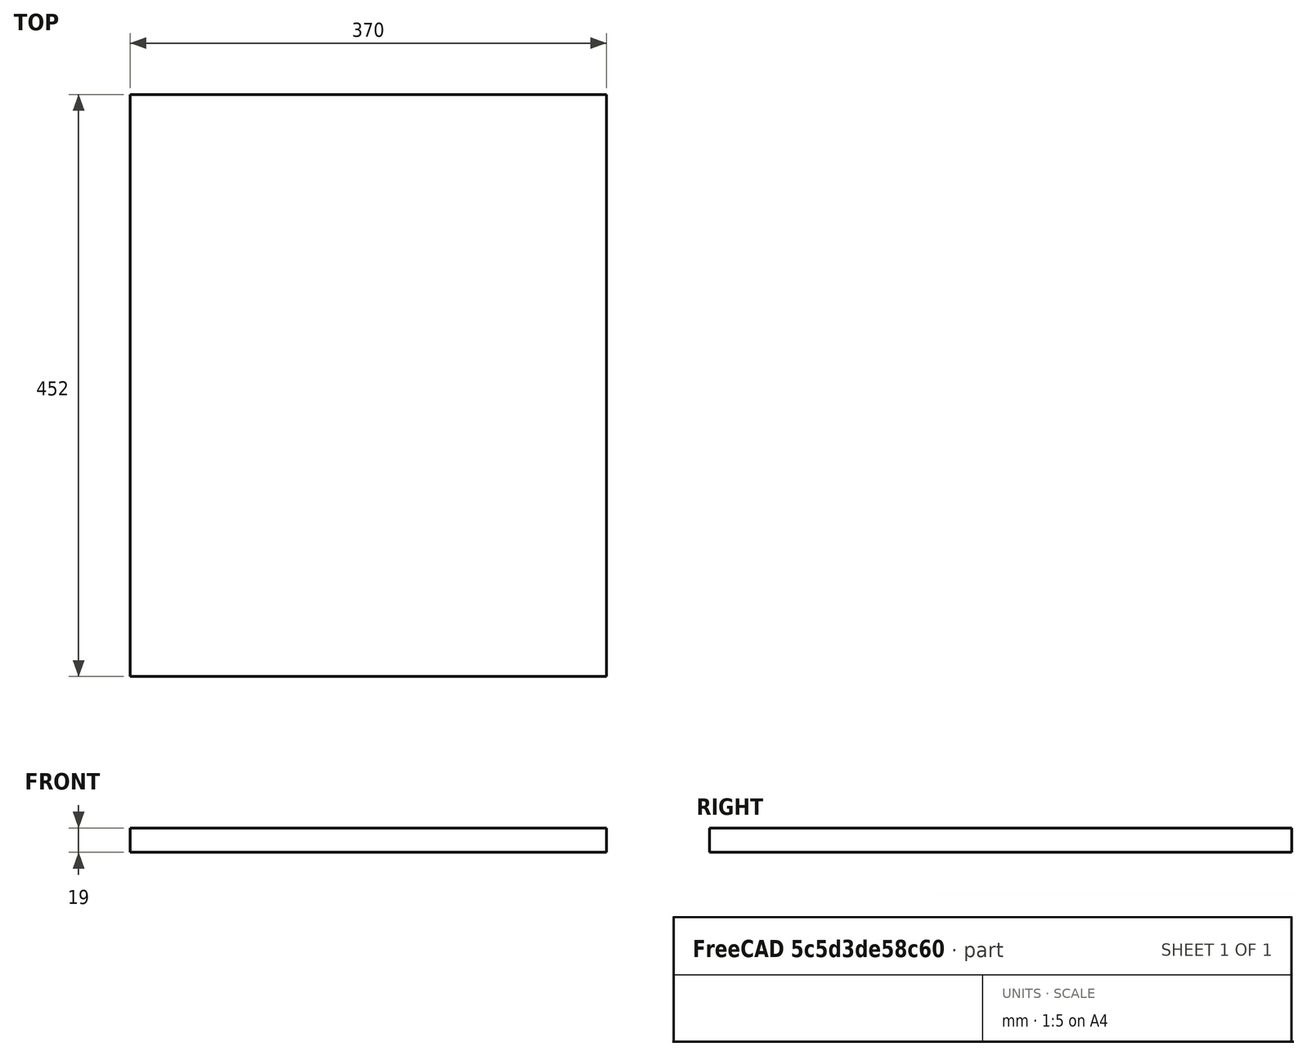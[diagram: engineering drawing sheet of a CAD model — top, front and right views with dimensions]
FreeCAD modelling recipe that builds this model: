
FCSTD DOCUMENT  (FreeCAD 0.20R29603 (Git))
Label: 500_Pedastil_Floor
License: All rights reserved
LicenseURL: http://en.wikipedia.org/wiki/All_rights_reserved
objects: Sketcher::SketchObject×2, PartDesign::Pad×1, Spreadsheet::Sheet×1, PartDesign::Body×1, App::Part×1
note: 5 computed .brp shape members not serialized (recipe doc carries the construction recipe); baked Part::Feature solids carry a one-line shape summary decoded from their .brp

FEATURE [Sketcher::SketchObject] Sketch
  FullyConstrained = false
  MapMode = 2
  expr: Constraints[5] = Spreadsheet.Depth
  expr: Constraints[6] = Spreadsheet.Width
  sketch-geometry (7):
    g0: LineSegment StartX=0 StartY=413.879 StartZ=0 EndX=0 EndY=452 EndZ=0
    g1: LineSegment StartX=0 StartY=452 StartZ=0 EndX=370 EndY=452 EndZ=0
    g2: LineSegment StartX=370 StartY=452 StartZ=0 EndX=370 EndY=0 EndZ=0
    g3: LineSegment StartX=370 StartY=0 StartZ=0 EndX=0 EndY=0 EndZ=0
    g4: LineSegment StartX=0 StartY=0 StartZ=0 EndX=0 EndY=413.879 EndZ=0
    g5: LineSegment StartX=0 StartY=0 StartZ=0 EndX=185 EndY=226 EndZ=0
    g6: LineSegment StartX=185 StartY=226 StartZ=0 EndX=370 EndY=452 EndZ=0
  constraints (18):
    c: Coincident(g1,g0)
    c: Horizontal(g1)
    c: Horizontal(g3)
    c: Coincident(g4,g3)
    c: Coincident(g3,g2)
    c: Distance(g1) = 370
    c: DistanceY(g2,g2) = 452
    c: Coincident(g1,g2)
    c: Coincident(g5,g3)
    c: Coincident(g6,g1)
    c: Equal(g6,g5)
    c: Coincident(g5,g6)
    c: Parallel(g5,g6)
    c: Vertical(g0)
    c: Vertical(g2)
    c: Coincident(g4,g0)
    c: Vertical(g4)
    c: Coincident(g3,g-1)
FEATURE [PartDesign::Pad] Pad
  AllowMultiFace = false
  Direction = (1,1,1)
  Length = 19
  Length2 = 100
  Profile = -> Sketch
  Reversed = true
  Type = 0
FEATURE [Spreadsheet::Sheet] Spreadsheet
  cells = B2=Dependancies; C2=Value; D2=Nominal; E2=Var; F2=Description; G2=FILE; B3=Side Wall pedistil; C3=19; B4=Sidewall Width; C4=415; B5=Front Wall thickness; C5=10; B8=BODY FLOOR; C8=Value; D8=Nominal; E8=Var; F8=Description; G8=FILE; B9=Orientation; C9=(0,0,1); F9=XY; B10=Z=; C10(T)=19; E10=.T; F10=Thichness Z; B11=Y=; C11(Width)==500 - 2 * C3 - 10; D11=500; E11=.W; F11=Width Y; B12=X=; C12(Depth)==D12 - 4 * C5 - 5; D12==+C4; E12=.D; F12=Depth X
FEATURE [Sketcher::SketchObject] Sketch001
  FullyConstrained = false
  MapMode = 5
  Placement = pos=(0,0,-19) rot=(1,0,0;3.14159rad)
  Support = -> [Pad]
  sketch-geometry (3):
    g0: LineSegment StartX=16.778 StartY=-210.88 StartZ=0 EndX=17.2836 EndY=-236.816 EndZ=0
    g1: LineSegment StartX=17.2836 StartY=-236.816 StartZ=0 EndX=84.9762 EndY=-236.816 EndZ=0
    g2: LineSegment StartX=84.9762 StartY=-236.816 StartZ=0 EndX=16.778 EndY=-210.88 EndZ=0
  constraints (4):
    c: Coincident(g0,g1)
    c: Horizontal(g1)
    c: Coincident(g1,g2)
    c: Coincident(g2,g0)
FEATURE [PartDesign::Body] PadBody
  Group = -> [Sketch,Pad]
  Origin = -> Origin001
  Tip = -> Pad
FEATURE [App::Part] Part
  Group = -> [PadBody]
  License = CC BY 3.0
  LicenseURL = http://creativecommons.org/licenses/by/3.0/
  Origin = -> Origin
